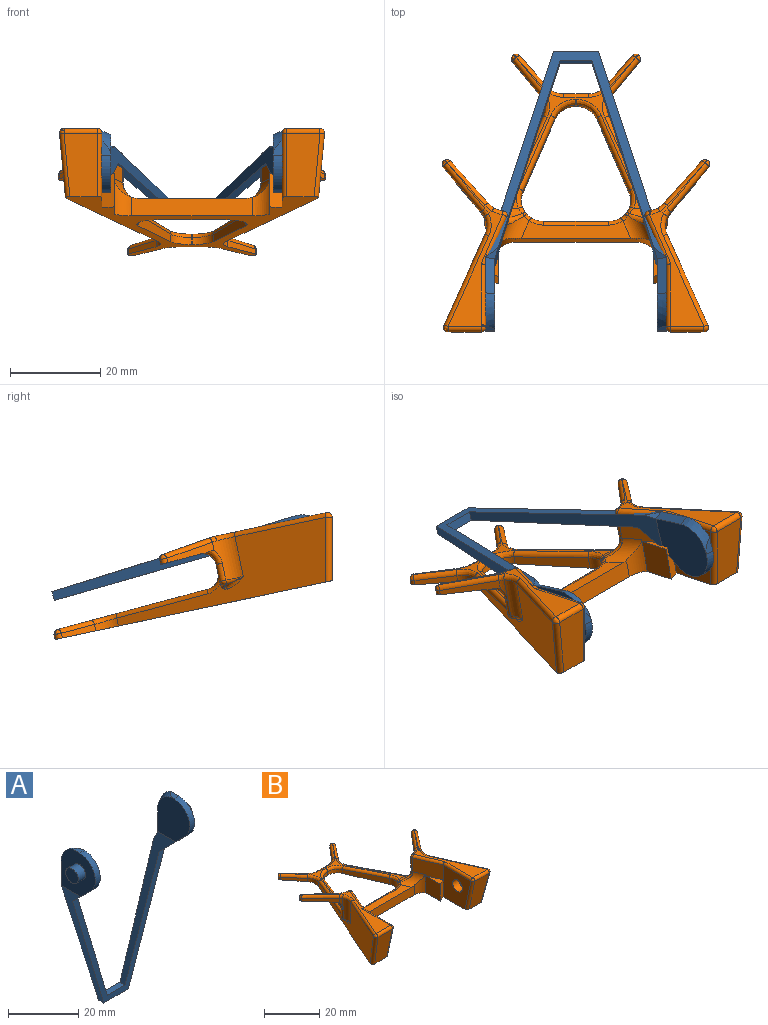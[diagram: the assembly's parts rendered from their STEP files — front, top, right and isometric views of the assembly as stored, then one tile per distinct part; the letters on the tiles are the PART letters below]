
ASSEMBLY  parts=2 mates=1
PART A: 28 faces, bbox 46x13.7x63.2 mm
  f0: plane 14.9x13.65mm, normal (1,0,0), area 150mm2, adj f2,f7,f10,f11,f18,f20,f26,f27
  f1: plane 14.9x13.65mm, normal (-1,0,0), area 150mm2, adj f3,f6,f10,f14,f16,f22,f24,f25
  f2: cone r=7.25mm half-angle=23deg, axis (1,0,0), area 18.3mm2, adj f0,f4,f18,f26
  f3: cone r=7.25mm half-angle=23deg, axis (-1,0,0), area 18.3mm2, adj f1,f5,f16,f25
  f4: plane 14.59x12.81mm, normal (-1,0,0), area 153.1mm2, adj f2,f7,f12,f18,f27
  f5: plane 14.59x12.81mm, normal (1,0,0), area 153.1mm2, adj f3,f6,f13,f16,f24
  f6: plane 8.78x8.78mm, normal (0,-0.71,-0.71), area 25.5mm2, adj f1,f5,f13,f14,f15,f24
  f7: plane 8.78x8.78mm, normal (0,-0.71,-0.71), area 25.5mm2, adj f0,f4,f11,f12,f15,f27
  f8: plane 10x2mm, normal (0,0,-1), area 20mm2, adj f10,f11,f14,f15
  f9: plane 7.07x2.05mm, normal (0,0,1), area 14.5mm2, adj f10,f12,f13,f15
  f10: plane 47.78x40mm, normal (0,1,0), area 208.1mm2, adj f0,f1,f8,f9,f11,f12,f13,f14
  f11: plane 47.47x15mm, normal (0.95,0,-0.3), area 139.1mm2, adj f0,f7,f8,f10,f15
  f12: plane 45.78x14.47mm, normal (-0.95,0,0.3), area 136.3mm2, adj f4,f7,f9,f10,f15,f19
  f13: plane 45.78x14.47mm, normal (0.95,0,0.3), area 136.3mm2, adj f5,f6,f9,f10,f15,f17
  f14: plane 47.47x15mm, normal (-0.95,0,-0.3), area 139.1mm2, adj f1,f6,f8,f10,f15
  f15: plane 42.66x36.96mm, normal (0,-1,-0.02), area 191.9mm2, adj f6,f7,f8,f9,f11,f12,f13,f14
  f16: plane 8.19x2mm, normal (0.39,0.92,0), area 17.8mm2, adj f1,f3,f5,f17
  f17: plane 2.82x2.6mm, normal (0.36,0.85,0.39), area 3.1mm2, adj f10,f13,f16
  f18: plane 8.19x2mm, normal (-0.39,0.92,0), area 17.8mm2, adj f0,f2,f4,f19
  f19: plane 2.82x2.6mm, normal (-0.36,0.85,0.39), area 3.1mm2, adj f10,f12,f18
  f20: cylinder r=2.5mm len=5mm, axis (-1,0,0), area 47.1mm2, adj f0,f21
  f21: plane 5x5mm, normal (1,0,0), area 19.6mm2, adj f20
  f22: cylinder r=2.5mm len=5mm, axis (1,0,0), area 47.1mm2, adj f1,f23
  f23: plane 5x5mm, normal (-1,0,0), area 19.6mm2, adj f22
  f24: cylinder r=6.4mm len=10.93mm, axis (-1,0,0), area 30.2mm2, adj f1,f5,f6,f25
  f25: plane 3.41x2mm, normal (0,0,1), area 4.5mm2, adj f1,f3,f24
  f26: plane 3.41x2mm, normal (0,0,1), area 4.5mm2, adj f0,f2,f27
  f27: cylinder r=6.4mm len=10.93mm, axis (-1,0,0), area 30.2mm2, adj f0,f4,f7,f26
PART B: 172 faces, bbox 59.6x66.1x15.6 mm
  f0: plane 7.66x2.76mm, normal (0,0,1), area 10.6mm2, adj f1,f3,f6
  f1: plane 7.5x2.76mm, normal (-0.39,-0.92,0), area 22.5mm2, adj f0,f2,f3,f25
  f2: plane 62.94x56.29mm, normal (0,0,-1), area 644.3mm2, adj f1,f3,f5,f7,f11,f14,f15,f16
  f3: plane 7.66x7.5mm, normal (1,0,0), area 57.4mm2, adj f0,f1,f2,f43
  f4: plane 10.95x6.5mm, normal (-0.92,-0.39,0), area 74.9mm2, adj f11,f40,f44,f58,f139,f145,f146,f147
  f5: plane 16.74x7.12mm, normal (0.92,-0.39,0), area 39.8mm2, adj f2,f45,f55,f63
  f6: plane 10.95x6.5mm, normal (0.92,-0.39,0), area 74.9mm2, adj f0,f25,f43,f57,f104,f152,f153,f154
  f7: plane 16.74x7.12mm, normal (-0.92,-0.39,0), area 39.8mm2, adj f2,f46,f56,f71
  f8: plane 10.98x8.86mm, normal (0.78,-0.62,0), area 19.6mm2, adj f33,f47,f60,f124,f125,f158
  f9: plane 10.98x8.86mm, normal (-0.78,-0.62,0), area 19.6mm2, adj f32,f54,f59,f108,f114,f163
  f10: plane 26.16x12.11mm, normal (0,0,1), area 76mm2, adj f34,f101,f104,f106,f112,f117,f118
  f11: plane 14.04x14mm, normal (-1,0,0), area 156.1mm2, adj f2,f4,f41,f133,f137,f170
  f12: plane 1.09x0.02mm, normal (0.62,0.78,0), area 0mm2, adj f33,f124,f130,f131
  f13: plane 9.95x8.48mm, normal (-0.76,0.65,0), area 19.5mm2, adj f33,f48,f60,f130,f136
  f14: plane 50.19x22.22mm, normal (0.92,0.4,0), area 378mm2, adj f2,f28,f47,f49,f98,f99,f126,f127
  f15: plane 7.58x6.06mm, normal (0.78,-0.62,0), area 12.3mm2, adj f2,f49,f94,f96
  f16: plane 1.07x0.02mm, normal (0.65,0.76,0), area 0mm2, adj f2,f91,f93,f94
  f17: plane 7.02x5.98mm, normal (-0.76,0.65,0), area 11.5mm2, adj f2,f50,f90,f91
  f18: plane 5.38x1.54mm, normal (0,1,0), area 8.3mm2, adj f2,f50,f51,f88
  f19: plane 7.02x5.98mm, normal (0.76,0.65,0), area 11.5mm2, adj f2,f51,f84,f86
  f20: plane 1.07x0.02mm, normal (-0.65,0.76,0), area 0mm2, adj f2,f81,f83,f84
  f21: plane 7.58x6.06mm, normal (-0.78,-0.62,0), area 12.3mm2, adj f2,f52,f80,f81
  f22: plane 9.95x8.48mm, normal (0.76,0.65,0), area 19.5mm2, adj f32,f53,f59,f102,f103
  f23: plane 1.09x0.02mm, normal (-0.62,0.78,0), area 0mm2, adj f32,f102,f108,f109
  f24: plane 50.19x22.22mm, normal (-0.92,0.4,0), area 378mm2, adj f2,f30,f52,f54,f77,f78,f113,f117
  f25: plane 14.04x14mm, normal (1,0,0), area 156.1mm2, adj f1,f2,f6,f106,f107,f169
  f26: plane 1.57x0.15mm, normal (0,-1,0), area 0.2mm2, adj f2,f55,f56,f67
  f27: plane 26.16x12.11mm, normal (0,0,1), area 76mm2, adj f31,f123,f126,f132,f137,f139,f140
  f28: plane 4.59x3.32mm, normal (0,1,0), area 9.4mm2, adj f14,f60,f62,f99,f147,f148,f159,f161
  f29: plane 34.57x31.08mm, normal (0,0.05,1), area 64.6mm2, adj f61,f62,f63,f64,f65,f67,f69,f71
  f30: plane 4.59x3.32mm, normal (0,1,0), area 9.4mm2, adj f24,f59,f61,f77,f154,f155,f164,f166
  f31: plane 11.93x10.11mm, normal (0.06,0.08,0.99), area 4.3mm2, adj f27,f122,f123,f125,f131,f136,f138,f140
  f32: plane 9.07x8.91mm, normal (0,-0.05,-1), area 24mm2, adj f9,f22,f23,f59,f102,f108
  f33: plane 9.07x8.91mm, normal (0,-0.05,-1), area 24mm2, adj f8,f12,f13,f60,f124,f130
  f34: plane 11.93x10.11mm, normal (-0.06,0.08,0.99), area 4.3mm2, adj f10,f100,f101,f103,f109,f114,f116,f118
  f35: plane 13.79x7.36mm, normal (0,-0.98,-0.21), area 94.7mm2, adj f2,f127,f132,f133
  f36: plane 13.79x7.36mm, normal (0,-0.98,-0.21), area 94.7mm2, adj f2,f107,f112,f113
  f37: plane 26.77x4.18mm, normal (0,-1,0), area 107.2mm2, adj f2,f39,f43,f44,f57,f58
  f38: plane 14.4x3mm, normal (0,1,0), area 43.2mm2, adj f2,f45,f46,f72
  f39: plane 24.24x3.95mm, normal (0,0,1), area 71.2mm2, adj f37,f57,f58,f70,f72,f74
  f40: plane 7.66x2.76mm, normal (0,0,1), area 10.6mm2, adj f4,f41,f42
  f41: plane 7.5x2.76mm, normal (0.39,-0.92,0), area 22.5mm2, adj f2,f11,f40,f42
  f42: plane 7.66x7.5mm, normal (-1,0,0), area 57.4mm2, adj f2,f40,f41,f44
  f43: cylinder r=5mm len=8mm, axis (0,0,-1), area 24.1mm2, adj f2,f3,f6,f37,f57
  f44: cylinder r=5mm len=8mm, axis (0,0,1), area 24.1mm2, adj f2,f4,f37,f42,f58
  f45: cylinder r=5mm len=6.96mm, axis (0,0,-1), area 28.9mm2, adj f2,f5,f38,f64,f66,f68,f70
  f46: cylinder r=5mm len=6.96mm, axis (0,0,1), area 28.9mm2, adj f2,f7,f38,f73,f74,f75,f76
  f47: cylinder r=5mm len=9mm, axis (0,0,-1), area 41.6mm2, adj f8,f14,f122,f123,f143,f158,f159
  f48: cylinder r=5mm len=4.67mm, axis (0,0,1), area 12.7mm2, adj f13,f60,f138,f140,f145,f146
  f49: cylinder r=5mm len=5.14mm, axis (0,0,1), area 8.8mm2, adj f2,f14,f15,f97
  f50: cylinder r=5mm len=3.81mm, axis (0,0,-1), area 6.4mm2, adj f2,f17,f18,f89
  f51: cylinder r=5mm len=3.81mm, axis (0,0,1), area 6.4mm2, adj f2,f18,f19,f87
  f52: cylinder r=5mm len=5.14mm, axis (0,0,-1), area 8.8mm2, adj f2,f21,f24,f79
  f53: cylinder r=5mm len=4.67mm, axis (0,0,-1), area 12.7mm2, adj f22,f59,f100,f101,f152,f153
  f54: cylinder r=5mm len=9mm, axis (0,0,1), area 41.6mm2, adj f9,f24,f116,f118,f121,f163,f164
  f55: cylinder r=5mm len=4.6mm, axis (0,0,-1), area 9.7mm2, adj f2,f5,f26,f65
  f56: cylinder r=5mm len=4.6mm, axis (0,0,1), area 9.7mm2, adj f2,f7,f26,f69
  f57: cylinder r=4mm len=9.42mm, axis (0.39,0.92,0), area 28.7mm2, adj f6,f37,f39,f43,f68,f155,f156
  f58: cylinder r=4mm len=9.42mm, axis (0.39,-0.92,0), area 28.7mm2, adj f4,f37,f39,f44,f76,f148,f149
  f59: cylinder r=3mm len=7.34mm, axis (1,0,0), area 11.2mm2, adj f9,f22,f30,f32,f53,f153,f163
  f60: cylinder r=3mm len=7.34mm, axis (1,0,0), area 11.2mm2, adj f8,f13,f28,f33,f48,f146,f158
  f61: cylinder r=3mm len=5.41mm, axis (1,0,0), area 13.2mm2, adj f29,f30,f66,f77,f156
  f62: cylinder r=3mm len=5.41mm, axis (1,0,0), area 13.2mm2, adj f28,f29,f75,f99,f149
  f63: cylinder r=1mm len=17.18mm, axis (-0.39,-0.92,0.05), area 29mm2, adj f5,f29,f64,f65
  f64: bspline ~4.56x1.4mm, area 6.6mm2, adj f29,f45,f63,f66
  f65: bspline ~5.64x4.34mm, area 10.1mm2, adj f29,f55,f63,f67
  f66: bspline ~2.53x2.36mm, area 2.2mm2, adj f45,f61,f64,f157
  f67: cylinder r=1mm len=1.05mm, axis (-1,0,0), area 0.2mm2, adj f26,f29,f65,f69
  f68: bspline ~2.62x2.53mm, area 2.2mm2, adj f45,f57,f70,f157
  f69: bspline ~6.69x4.34mm, area 10.1mm2, adj f29,f56,f67,f71
  f70: torus R=6mm, axis (0,0,-1), area 4.8mm2, adj f39,f45,f68,f72
  f71: cylinder r=1mm len=17.18mm, axis (-0.39,0.92,-0.05), area 29mm2, adj f7,f29,f69,f73
  f72: cylinder r=1mm len=14.4mm, axis (-1,0,0), area 22.6mm2, adj f38,f39,f70,f74
  f73: bspline ~4.56x1.4mm, area 6.6mm2, adj f29,f46,f71,f75
  f74: torus R=6mm, axis (0,0,-1), area 4.8mm2, adj f39,f46,f72,f76
  f75: bspline ~2.53x2.36mm, area 2.2mm2, adj f46,f62,f73,f150
  f76: bspline ~2.62x2.53mm, area 2.2mm2, adj f46,f58,f74,f150
  f77: bspline ~3.99x3.79mm, area 6mm2, adj f24,f30,f61,f78
  f78: cylinder r=1mm len=21.16mm, axis (-0.4,-0.91,0.05), area 35.3mm2, adj f24,f29,f77,f79
  f79: bspline ~6.16x2.1mm, area 9.2mm2, adj f29,f52,f78,f80
  f80: cylinder r=1mm len=8.26mm, axis (-0.62,0.78,-0.04), area 15.6mm2, adj f21,f29,f79,f82
  f81: cylinder r=1mm len=1.39mm, axis (0,0,-1), area 1.7mm2, adj f2,f20,f21,f82
  f82: sphere r=1mm, area 1.8mm2, adj f80,f81,f83
  f83: cylinder r=1mm len=1mm, axis (0.76,0.65,-0.03), area 0mm2, adj f20,f29,f82,f85
  f84: cylinder r=1mm len=1.41mm, axis (0,0,-1), area 1.7mm2, adj f2,f19,f20,f85
  f85: sphere r=1mm, area 1mm2, adj f83,f84,f86
  f86: cylinder r=1mm len=7.62mm, axis (0.65,-0.76,0.04), area 14.2mm2, adj f19,f29,f85,f87
  f87: bspline ~4.57x2.71mm, area 7.1mm2, adj f29,f51,f86,f88
  f88: cylinder r=1mm len=5.38mm, axis (1,0,0), area 8.2mm2, adj f18,f29,f87,f89
  f89: bspline ~4.57x2.71mm, area 7.1mm2, adj f29,f50,f88,f90
  f90: cylinder r=1mm len=7.62mm, axis (0.65,0.76,-0.04), area 14.2mm2, adj f17,f29,f89,f92
  f91: cylinder r=1mm len=1.41mm, axis (0,0,-1), area 1.7mm2, adj f2,f16,f17,f92
  f92: sphere r=1mm, area 1mm2, adj f90,f91,f93
  f93: cylinder r=1mm len=1mm, axis (0.76,-0.65,0.03), area 0mm2, adj f16,f29,f92,f95
  f94: cylinder r=1mm len=1.39mm, axis (0,0,-1), area 1.7mm2, adj f2,f15,f16,f95
  f95: sphere r=1mm, area 1.8mm2, adj f93,f94,f96
  f96: cylinder r=1mm len=8.26mm, axis (-0.62,-0.78,0.04), area 15.6mm2, adj f15,f29,f95,f97
  f97: bspline ~6.16x2.1mm, area 9.2mm2, adj f29,f49,f96,f98
  f98: cylinder r=1mm len=21.16mm, axis (0.4,-0.91,0.05), area 35.3mm2, adj f14,f29,f97,f99
  f99: bspline ~3.99x3.79mm, area 6mm2, adj f14,f28,f62,f98
  f100: bspline ~2.19x1.91mm, area 2.9mm2, adj f34,f53,f101,f103
  f101: torus R=6mm, axis (0,0,1), area 3.4mm2, adj f10,f34,f53,f100,f151
  f102: cylinder r=1mm len=1.39mm, axis (0,0,-1), area 1.7mm2, adj f22,f23,f32,f105
  f103: cylinder r=1mm len=10.5mm, axis (-0.65,0.76,-0.1), area 20.5mm2, adj f22,f34,f100,f105
  f104: cylinder r=1mm len=11.53mm, axis (-0.39,-0.92,0), area 18.9mm2, adj f6,f10,f106,f151
  f105: sphere r=1mm, area 0.9mm2, adj f102,f103,f109
  f106: cylinder r=1mm len=14.25mm, axis (0,-1,0), area 22.2mm2, adj f10,f25,f104,f110
  f107: cylinder r=1mm len=14.21mm, axis (0,0.21,-0.98), area 22.3mm2, adj f2,f25,f36,f110
  f108: cylinder r=1mm len=1.41mm, axis (0,0,-1), area 1.6mm2, adj f9,f23,f32,f111
  f109: cylinder r=1mm len=1mm, axis (-0.78,-0.62,0), area 0mm2, adj f23,f34,f105,f111
  f110: sphere r=1mm, area 2.4mm2, adj f106,f107,f112
  f111: sphere r=1mm, area 1mm2, adj f108,f109,f114
  f112: cylinder r=1mm len=7.36mm, axis (1,0,0), area 13.1mm2, adj f10,f36,f110,f115
  f113: cylinder r=1mm len=14.23mm, axis (-0.09,-0.21,0.97), area 28.2mm2, adj f2,f24,f36,f115
  f114: cylinder r=1mm len=11.31mm, axis (0.62,-0.78,0.1), area 21.4mm2, adj f9,f34,f111,f116
  f115: sphere r=1mm, area 1.5mm2, adj f112,f113,f117
  f116: bspline ~1.79x1.51mm, area 2.1mm2, adj f34,f54,f114,f118
  f117: cylinder r=1mm len=20.99mm, axis (0.4,0.92,0), area 35.3mm2, adj f10,f24,f115,f118
  f118: torus R=6mm, axis (0,0,1), area 7.1mm2, adj f10,f34,f54,f116,f117
  f119: cylinder r=1mm len=1.05mm, axis (-0.4,-0.92,0), area 0.5mm2, adj f24,f120,f167
  f120: bspline ~4.99x2.07mm, area 3.8mm2, adj f24,f119,f121,f166
  f121: torus R=6mm, axis (0,0,1), area 3.1mm2, adj f54,f120,f165
  f122: bspline ~1.79x1.51mm, area 2.1mm2, adj f31,f47,f123,f125
  f123: torus R=6mm, axis (0,0,1), area 7.1mm2, adj f27,f31,f47,f122,f126
  f124: cylinder r=1mm len=1.41mm, axis (0,0,-1), area 1.6mm2, adj f8,f12,f33,f128
  f125: cylinder r=1mm len=11.31mm, axis (0.62,0.78,-0.1), area 21.4mm2, adj f8,f31,f122,f128
  f126: cylinder r=1mm len=20.99mm, axis (-0.4,0.92,0), area 35.3mm2, adj f14,f27,f123,f129
  f127: cylinder r=1mm len=14.23mm, axis (-0.09,0.21,-0.97), area 28.2mm2, adj f2,f14,f35,f129
  f128: sphere r=1mm, area 1.5mm2, adj f124,f125,f131
  f129: sphere r=1mm, area 2.3mm2, adj f126,f127,f132
  f130: cylinder r=1mm len=1.39mm, axis (0,0,-1), area 1.7mm2, adj f12,f13,f33,f134
  f131: cylinder r=1mm len=1mm, axis (-0.78,0.62,0), area 0mm2, adj f12,f31,f128,f134
  f132: cylinder r=1mm len=7.36mm, axis (-1,0,0), area 13.1mm2, adj f27,f35,f129,f135
  f133: cylinder r=1mm len=14.21mm, axis (0,-0.21,0.98), area 22.3mm2, adj f2,f11,f35,f135
  f134: sphere r=1mm, area 0.9mm2, adj f130,f131,f136
  f135: sphere r=1mm, area 1.7mm2, adj f132,f133,f137
  f136: cylinder r=1mm len=10.5mm, axis (-0.65,-0.76,0.1), area 20.5mm2, adj f13,f31,f134,f138
  f137: cylinder r=1mm len=14.25mm, axis (0,1,0), area 22.2mm2, adj f11,f27,f135,f139
  f138: bspline ~2.19x1.91mm, area 2.9mm2, adj f31,f48,f136,f140
  f139: cylinder r=1mm len=11.53mm, axis (-0.39,0.92,0), area 18.9mm2, adj f4,f27,f137,f144
  f140: torus R=6mm, axis (0,0,1), area 3.4mm2, adj f27,f31,f48,f138,f144
  f141: cylinder r=1mm len=1.05mm, axis (-0.4,0.92,0), area 0.5mm2, adj f14,f142,f162
  f142: bspline ~4.99x2.07mm, area 3.8mm2, adj f14,f141,f143,f161
  f143: torus R=6mm, axis (0,0,-1), area 3.1mm2, adj f47,f142,f160
  f144: sphere r=1mm, area 2.5mm2, adj f139,f140,f145
  f145: cylinder r=1mm len=4.67mm, axis (0,0,1), area 8.6mm2, adj f4,f48,f144,f146
  f146: bspline ~1.55x1.53mm, area 1mm2, adj f4,f48,f60,f145,f147
  f147: cylinder r=1mm len=1.39mm, axis (0,0,-1), area 1.7mm2, adj f4,f28,f146,f148
  f148: bspline ~1.65x1.51mm, area 1.9mm2, adj f28,f58,f147,f149
  f149: bspline ~5.26x3.47mm, area 7mm2, adj f58,f62,f148,f150
  f150: sphere r=1mm, area 0.8mm2, adj f75,f76,f149
  f151: sphere r=1mm, area 1.3mm2, adj f101,f104,f152
  f152: cylinder r=1mm len=4.67mm, axis (0,0,-1), area 8.6mm2, adj f6,f53,f151,f153
  f153: bspline ~1.55x1.53mm, area 1mm2, adj f6,f53,f59,f152,f154
  f154: cylinder r=1mm len=1.39mm, axis (0,0,1), area 1.7mm2, adj f6,f30,f153,f155
  f155: bspline ~2.37x1.65mm, area 1.9mm2, adj f30,f57,f154,f156
  f156: bspline ~5.26x3.47mm, area 7mm2, adj f57,f61,f155,f157
  f157: sphere r=1mm, area 0.7mm2, adj f66,f68,f156
  f158: bspline ~4.79x4.64mm, area 8.6mm2, adj f8,f47,f60,f159
  f159: cylinder r=1mm len=3.84mm, axis (0,0,-1), area 7.6mm2, adj f28,f47,f158,f160
  f160: sphere r=1mm, area 1mm2, adj f143,f159,f161
  f161: bspline ~1.31x1.25mm, area 0.3mm2, adj f28,f142,f160,f162
  f162: bspline ~1.97x1.96mm, area 2mm2, adj f14,f28,f141,f161
  f163: bspline ~4.79x4.64mm, area 8.6mm2, adj f9,f54,f59,f164
  f164: cylinder r=1mm len=3.84mm, axis (0,0,1), area 7.6mm2, adj f30,f54,f163,f165
  f165: sphere r=1mm, area 1.8mm2, adj f121,f164,f166
  f166: bspline ~1.31x1.25mm, area 0.3mm2, adj f30,f120,f165,f167
  f167: bspline ~1.97x1.96mm, area 2mm2, adj f24,f30,f119,f166
  f168: plane 5x5mm, normal (1,0,0), area 19.6mm2, adj f169
  f169: cylinder r=2.5mm len=5mm, axis (-1,0,0), area 47.1mm2, adj f25,f168
  f170: cylinder r=2.5mm len=5mm, axis (-1,0,0), area 47.1mm2, adj f11,f171
  f171: plane 5x5mm, normal (-1,0,0), area 19.6mm2, adj f170
PLACE A rot(axis=(1,0,0),72.6deg) t=(-24.37,12.22,-10.16)mm
PLACE B rot(axis=(-1,0,0),12deg) t=(-24.37,-3.12,-6.61)mm
MATE revolute B.f169 <-> A.f2  axis (1,0,0) through (-47.37,6.5,0.03)mm
